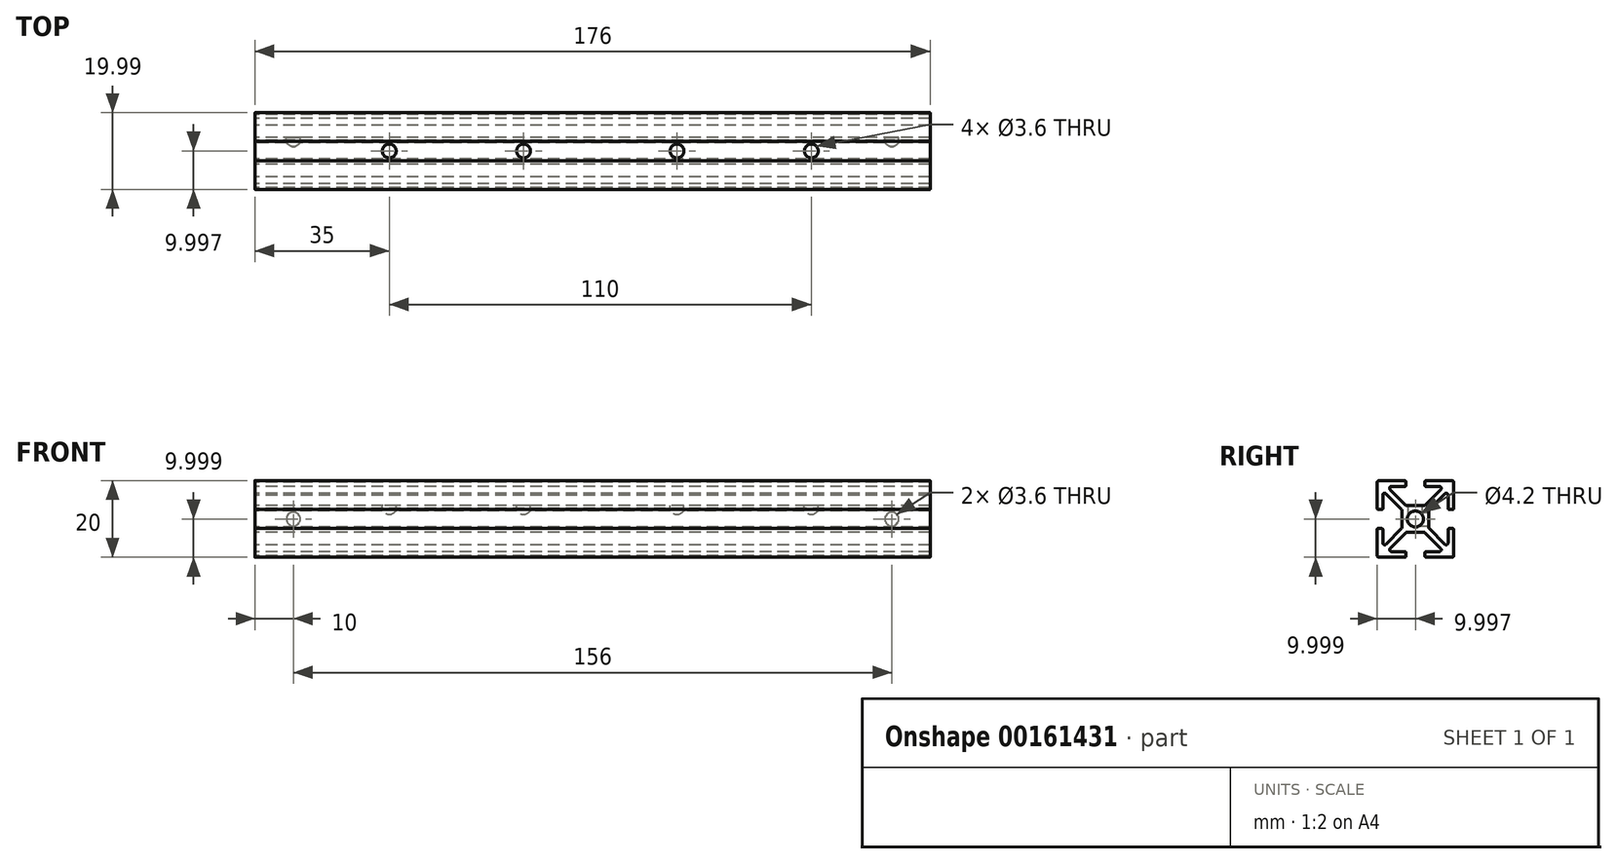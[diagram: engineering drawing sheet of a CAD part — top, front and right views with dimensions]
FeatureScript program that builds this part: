
annotation { "Feature Type Name" : "Feature", "Feature Type Description" : "" }
export const myFeature = defineFeature(function(context is Context, id is Id, definition is map)
    precondition{}
    {
        {
            var Q0;
            Q0=qCreatedBy(makeId("Right.planeOp"),FACE);
            var sketch = newSketch(context, id + "F0", { "sketchPlane" : qUnion([Q0])});
            skLineSegment(sketch, "E0.top", {"start": v(-10.52, -10.37) * mm, "end": v(-10.51, -10.37) * mm});
            skLineSegment(sketch, "E0.right", {"start": v(9.48, 9.63) * mm, "end": v(9.48, 9.63) * mm});
            skLineSegment(sketch, "E1.bottom", {"start": v(-3.26, 9.63) * mm, "end": v(-10.01, 9.63) * mm});
            skLineSegment(sketch, "E1.top", {"start": v(8.99, -10.37) * mm, "end": v(2.25, -10.37) * mm});
            skLineSegment(sketch, "E1.left", {"start": v(9.49, 9.13) * mm, "end": v(9.49, 2.38) * mm});
            skLineSegment(sketch, "E1.right", {"start": v(-10.51, -3.12) * mm, "end": v(-10.51, -9.87) * mm});
            skLineSegment(sketch, "E2", {"start": v(-10.51, 9.63) * mm, "end": v(-10.01, 9.13) * mm});
            skLineSegment(sketch, "E3", {"start": v(9.49, 9.63) * mm, "end": v(8.99, 9.13) * mm});
            skCircle(sketch, "E4", {"center": v(-0.51, -0.37) * mm, "radius": 2.1 * mm});
            skLineSegment(sketch, "E5.left", {"start": v(-3.01, 9.38) * mm, "end": v(-3.01, 8.38) * mm});
            skLineSegment(sketch, "E5.right", {"start": v(1.99, 9.38) * mm, "end": v(1.99, 8.38) * mm});
            skLineSegment(sketch, "E6", {"start": v(-4.01, 1.97) * mm, "end": v(-4.01, -2.7) * mm});
            skLineSegment(sketch, "E7", {"start": v(2.99, 1.97) * mm, "end": v(2.99, -2.7) * mm});
            skLineSegment(sketch, "E8", {"start": v(-6.75, -8.87) * mm, "end": v(-3.26, -8.87) * mm});
            skLineSegment(sketch, "E9", {"start": v(-9.01, -3.12) * mm, "end": v(-9.01, -6.6) * mm});
            skLineSegment(sketch, "E10", {"start": v(7.99, 5.86) * mm, "end": v(7.99, 2.38) * mm});
            skLineSegment(sketch, "E11", {"start": v(-6.75, 8.13) * mm, "end": v(-3.26, 8.13) * mm});
            skLineSegment(sketch, "E12.bottom", {"start": v(8.24, 2.13) * mm, "end": v(9.24, 2.13) * mm});
            skLineSegment(sketch, "E12.top", {"start": v(-10.26, -2.87) * mm, "end": v(-9.26, -2.87) * mm});
            skPoint(sketch, "E12.middle", {"position": v(9.49, -0.37) * mm});
            skLineSegment(sketch, "E13", {"start": v(-7.1, 7.28) * mm, "end": v(-3.03, 3.2) * mm});
            skLineSegment(sketch, "E14", {"start": v(2, -3.94) * mm, "end": v(6.07, -8.02) * mm});
            skLineSegment(sketch, "E15", {"start": v(6.07, 7.28) * mm, "end": v(2, 3.2) * mm});
            skLineSegment(sketch, "E16", {"start": v(-3.03, -3.94) * mm, "end": v(-7.1, -8.02) * mm});
            skArc(sketch, "E17.filletArc", {"start": v(-6.75, 8.13) * mm, "mid": v(-7.2, 7.82) * mm, "end": v(-7.1, 7.28) * mm});
            skPoint(sketch, "E18.newPointB", {"position": v(9.49, 8.13) * mm});
            skArc(sketch, "E18.filletArc", {"start": v(6.07, 7.28) * mm, "mid": v(6.18, 7.82) * mm, "end": v(5.72, 8.13) * mm});
            skArc(sketch, "E19.filletArc", {"start": v(7.99, 5.86) * mm, "mid": v(7.68, 6.32) * mm, "end": v(7.13, 6.22) * mm});
            skArc(sketch, "E20.filletArc", {"start": v(7.13, -6.96) * mm, "mid": v(7.68, -7.06) * mm, "end": v(7.99, -6.6) * mm});
            skArc(sketch, "E21.filletArc", {"start": v(5.72, -8.87) * mm, "mid": v(6.18, -8.56) * mm, "end": v(6.07, -8.02) * mm});
            skArc(sketch, "E22.filletArc", {"start": v(-7.1, -8.02) * mm, "mid": v(-7.2, -8.56) * mm, "end": v(-6.75, -8.87) * mm});
            skArc(sketch, "E23.filletArc", {"start": v(-9.01, -6.6) * mm, "mid": v(-8.7, -7.06) * mm, "end": v(-8.16, -6.96) * mm});
            skArc(sketch, "E24.filletArc", {"start": v(-8.16, 6.22) * mm, "mid": v(-8.73, 6.31) * mm, "end": v(-9, 5.8) * mm});
            skPoint(sketch, "E25.visualSharp", {"position": v(-10.51, 9.63) * mm});
            skArc(sketch, "E25.filletArc", {"start": v(-10.01, 9.63) * mm, "mid": v(-10.37, 9.48) * mm, "end": v(-10.51, 9.13) * mm});
            skPoint(sketch, "E26.visualSharp", {"position": v(9.49, 9.63) * mm});
            skArc(sketch, "E26.filletArc", {"start": v(9.49, 9.13) * mm, "mid": v(9.34, 9.48) * mm, "end": v(8.99, 9.63) * mm});
            skPoint(sketch, "E27.visualSharp", {"position": v(9.49, -10.37) * mm});
            skArc(sketch, "E27.filletArc", {"start": v(8.99, -10.37) * mm, "mid": v(9.34, -10.22) * mm, "end": v(9.49, -9.87) * mm});
            skPoint(sketch, "E28.visualSharp", {"position": v(-10.51, -10.37) * mm});
            skArc(sketch, "E28.filletArc", {"start": v(-10.51, -9.87) * mm, "mid": v(-10.37, -10.22) * mm, "end": v(-10.01, -10.37) * mm});
            skArc(sketch, "E29.filletArc", {"start": v(-3.26, 8.13) * mm, "mid": v(-3.09, 8.2) * mm, "end": v(-3.01, 8.38) * mm});
            skArc(sketch, "E30.filletArc", {"start": v(-9.01, -3.12) * mm, "mid": v(-9.09, -2.94) * mm, "end": v(-9.26, -2.87) * mm});
            skArc(sketch, "E31.filletArc", {"start": v(-3.01, 9.38) * mm, "mid": v(-3.09, 9.56) * mm, "end": v(-3.26, 9.63) * mm});
            skLineSegment(sketch, "E32", {"start": v(2.24, 9.63) * mm, "end": v(8.99, 9.63) * mm});
            skLineSegment(sketch, "E33", {"start": v(5.72, 8.13) * mm, "end": v(2.24, 8.13) * mm});
            skLineSegment(sketch, "E34", {"start": v(-9, 5.8) * mm, "end": v(-9, 2.38) * mm});
            skLineSegment(sketch, "E35", {"start": v(8.24, -2.87) * mm, "end": v(9.24, -2.87) * mm});
            skPoint(sketch, "E36.visualSharp", {"position": v(1.99, 8.13) * mm});
            skArc(sketch, "E36.filletArc", {"start": v(1.99, 8.38) * mm, "mid": v(2.06, 8.2) * mm, "end": v(2.24, 8.13) * mm});
            skPoint(sketch, "E37.visualSharp", {"position": v(1.99, 9.63) * mm});
            skArc(sketch, "E37.filletArc", {"start": v(2.24, 9.63) * mm, "mid": v(2.06, 9.56) * mm, "end": v(1.99, 9.38) * mm});
            skPoint(sketch, "E38.newPointB", {"position": v(-10.51, 2.13) * mm});
            skArc(sketch, "E38.filletArc", {"start": v(7.99, 2.38) * mm, "mid": v(8.06, 2.2) * mm, "end": v(8.24, 2.13) * mm});
            skLineSegment(sketch, "E39", {"start": v(7.99, -3.12) * mm, "end": v(7.99, -6.6) * mm});
            skPoint(sketch, "E40.visualSharp", {"position": v(7.99, -2.87) * mm});
            skArc(sketch, "E40.filletArc", {"start": v(8.24, -2.87) * mm, "mid": v(8.06, -2.94) * mm, "end": v(7.99, -3.12) * mm});
            skArc(sketch, "E41.filletArc", {"start": v(9.24, 2.13) * mm, "mid": v(9.41, 2.2) * mm, "end": v(9.49, 2.38) * mm});
            skLineSegment(sketch, "E42", {"start": v(9.49, -3.12) * mm, "end": v(9.49, -9.87) * mm});
            skPoint(sketch, "E43.visualSharp", {"position": v(9.49, -2.87) * mm});
            skArc(sketch, "E43.filletArc", {"start": v(9.49, -3.12) * mm, "mid": v(9.41, -2.94) * mm, "end": v(9.24, -2.87) * mm});
            skLineSegment(sketch, "E44", {"start": v(-9.26, 2.13) * mm, "end": v(-10.26, 2.13) * mm});
            skPoint(sketch, "E45.visualSharp", {"position": v(-9, 2.13) * mm});
            skArc(sketch, "E45.filletArc", {"start": v(-9.26, 2.13) * mm, "mid": v(-9.08, 2.2) * mm, "end": v(-9, 2.38) * mm});
            skPoint(sketch, "E46.newPointA", {"position": v(-10.51, -2.87) * mm});
            skArc(sketch, "E46.filletArc", {"start": v(-10.26, -2.87) * mm, "mid": v(-10.44, -2.94) * mm, "end": v(-10.51, -3.12) * mm});
            skLineSegment(sketch, "E47", {"start": v(-10.51, 2.38) * mm, "end": v(-10.51, 9.13) * mm});
            skArc(sketch, "E48.filletArc", {"start": v(-10.51, 2.38) * mm, "mid": v(-10.44, 2.2) * mm, "end": v(-10.26, 2.13) * mm});
            skPoint(sketch, "E49.newPointB", {"position": v(-3.01, 2.13) * mm});
            skLineSegment(sketch, "E50", {"start": v(7.13, -6.96) * mm, "end": v(3.06, -2.88) * mm});
            skPoint(sketch, "E50.endSnap0", {"position": v(2.99, -1.12) * mm});
            skPoint(sketch, "E51.newPointA", {"position": v(2.99, -2.8) * mm});
            skPoint(sketch, "E51.newPointB", {"position": v(2.99, -10.37) * mm});
            skArc(sketch, "E51.filletArc", {"start": v(2.99, -2.7) * mm, "mid": v(3, -2.8) * mm, "end": v(3.06, -2.88) * mm});
            skLineSegment(sketch, "E52", {"start": v(-2.85, -3.87) * mm, "end": v(1.82, -3.87) * mm});
            skArc(sketch, "E53.filletArc", {"start": v(2, -3.94) * mm, "mid": v(1.92, -3.89) * mm, "end": v(1.82, -3.87) * mm});
            skArc(sketch, "E54.filletArc", {"start": v(-2.85, -3.87) * mm, "mid": v(-2.94, -3.89) * mm, "end": v(-3.03, -3.94) * mm});
            skLineSegment(sketch, "E55", {"start": v(-8.16, -6.96) * mm, "end": v(-4.09, -2.88) * mm});
            skLineSegment(sketch, "E56", {"start": v(-8.16, 6.22) * mm, "end": v(-4.09, 2.14) * mm});
            skArc(sketch, "E57.filletArc", {"start": v(-4.01, 1.97) * mm, "mid": v(-4.03, 2.06) * mm, "end": v(-4.09, 2.14) * mm});
            skArc(sketch, "E58.filletArc", {"start": v(-4.09, -2.88) * mm, "mid": v(-4.03, -2.8) * mm, "end": v(-4.01, -2.7) * mm});
            skLineSegment(sketch, "E59", {"start": v(7.13, 6.22) * mm, "end": v(3.06, 2.14) * mm});
            skPoint(sketch, "E60.newPointB", {"position": v(2.99, 8.13) * mm});
            skArc(sketch, "E60.filletArc", {"start": v(3.06, 2.14) * mm, "mid": v(3, 2.06) * mm, "end": v(2.99, 1.97) * mm});
            skLineSegment(sketch, "E61", {"start": v(-2.85, 3.13) * mm, "end": v(1.82, 3.13) * mm});
            skArc(sketch, "E62.filletArc", {"start": v(-3.03, 3.2) * mm, "mid": v(-2.94, 3.15) * mm, "end": v(-2.85, 3.13) * mm});
            skArc(sketch, "E63.filletArc", {"start": v(1.82, 3.13) * mm, "mid": v(1.92, 3.15) * mm, "end": v(2, 3.2) * mm});
            skPoint(sketch, "E64.orphan", {"position": v(-3.01, 9.63) * mm});
            skPoint(sketch, "E65.orphan", {"position": v(-0.51, 9.63) * mm});
            skPoint(sketch, "E66.orphan", {"position": v(-10.51, -0.37) * mm});
            skLineSegment(sketch, "E67.trimOffspring", {"start": v(8.99, -9.87) * mm, "end": v(9.49, -10.37) * mm});
            skLineSegment(sketch, "E68.trimOffspring", {"start": v(-10.01, -9.87) * mm, "end": v(-10.51, -10.37) * mm});
            skPoint(sketch, "E69.trimOffspring.end.orphan", {"position": v(-0.51, -10.37) * mm});
            skLineSegment(sketch, "E70", {"start": v(2, 8.88) * mm, "end": v(2, 8.3) * mm});
            skPoint(sketch, "E70.startSnap0", {"position": v(1.99, 8.88) * mm});
            skLineSegment(sketch, "E71", {"start": v(-3.01, 8.88) * mm, "end": v(-3.01, 8.38) * mm});
            skPoint(sketch, "E72.start.orphan", {"position": v(-2.85, -8.87) * mm});
            skLineSegment(sketch, "E73.trimOffspring", {"start": v(2.25, -8.87) * mm, "end": v(5.72, -8.87) * mm});
            skLineSegment(sketch, "E74.trimOffspring", {"start": v(-3.26, -10.37) * mm, "end": v(-10.01, -10.37) * mm});
            skLineSegment(sketch, "E75.trimOffspring", {"start": v(2, -9.12) * mm, "end": v(2, -10.12) * mm});
            skLineSegment(sketch, "E76.trimOffspring", {"start": v(-3.01, -9.12) * mm, "end": v(-3.01, -10.12) * mm});
            skArc(sketch, "E77.filletArc", {"start": v(-3.01, -9.12) * mm, "mid": v(-3.09, -8.94) * mm, "end": v(-3.26, -8.87) * mm});
            skPoint(sketch, "E78.visualSharp", {"position": v(2, -8.87) * mm});
            skArc(sketch, "E78.filletArc", {"start": v(2.25, -8.87) * mm, "mid": v(2.07, -8.94) * mm, "end": v(2, -9.12) * mm});
            skPoint(sketch, "E79.visualSharp", {"position": v(-3.01, -10.37) * mm});
            skArc(sketch, "E79.filletArc", {"start": v(-3.26, -10.37) * mm, "mid": v(-3.09, -10.3) * mm, "end": v(-3.01, -10.12) * mm});
            skPoint(sketch, "E80.visualSharp", {"position": v(2, -10.37) * mm});
            skArc(sketch, "E80.filletArc", {"start": v(2, -10.12) * mm, "mid": v(2.07, -10.3) * mm, "end": v(2.25, -10.37) * mm});
            skLineSegment(sketch, "E81.trimOffspring", {"start": v(9.48, -3.08) * mm, "end": v(9.48, -9.93) * mm});
            skLineSegment(sketch, "E82.trimOffspring", {"start": v(2.24, -10.37) * mm, "end": v(9, -10.37) * mm});
            skLineSegment(sketch, "E83", {"start": v(-10.51, -9.87) * mm, "end": v(-10.51, -3.12) * mm});
            skLineSegment(sketch, "E84", {"start": v(-10.51, 9.13) * mm, "end": v(-10.51, 2.38) * mm});
            skLineSegment(sketch, "E85.trimOffspring", {"start": v(9.48, 9.19) * mm, "end": v(9.48, 2.34) * mm});
            skLineSegment(sketch, "E86.trimOffspring", {"start": v(9.48, -10.37) * mm, "end": v(9.48, -10.37) * mm});
            skLineSegment(sketch, "E87.trimOffspring", {"start": v(-10.03, -10.37) * mm, "end": v(-3.25, -10.37) * mm});
            skSolve(sketch);
        }
        {
            var Q0;
            Q0=makeQuery(id+"F0.imprint","IMPRINT",FACE,{"disambiguationData":[TD([[makeQuery(id+"F0.imprint","IMPRINT",EDGE,{"derivedFrom":sQuery(id+"F0.wireOp",EDGE,"E4")}),-1.0]])]});
            extrude(context, id + "F1", {"entities" : qUnion([Q0]), "depth" : 176 * mm});
        }
        {
            var Q0;
            Q0=makeQuery(id+"F1.opExtrude","SWEPT_FACE",FACE,{"disambiguationData":[OSD([sQuery(id+"F0.wireOp",EDGE,"E61")])]});
            var sketch = newSketch(context, id + "F2", { "sketchPlane" : qUnion([Q0])});
            skPoint(sketch, "E88", {"position": v(0, -0.51) * mm});
            skLineSegment(sketch, "E89", {"start": v(0, -0.51) * mm, "end": v(145, -0.51) * mm});
            skPoint(sketch, "E90", {"position": v(176, -0.51) * mm});
            skPoint(sketch, "E91", {"position": v(145, -0.51) * mm});
            skPoint(sketch, "E92", {"position": v(35, -0.51) * mm});
            skPoint(sketch, "E93", {"position": v(70, -0.51) * mm});
            skPoint(sketch, "E94", {"position": v(110, -0.51) * mm});
            skCircle(sketch, "E95", {"center": v(35, -0.51) * mm, "radius": 1.8 * mm});
            skCircle(sketch, "E96", {"center": v(70, -0.51) * mm, "radius": 1.8 * mm});
            skCircle(sketch, "E97", {"center": v(110, -0.51) * mm, "radius": 1.8 * mm});
            skCircle(sketch, "E98", {"center": v(145, -0.51) * mm, "radius": 1.8 * mm});
            skSolve(sketch);
        }
        {
            var Q0;
            Q0 = qSketchRegion(id + "F2", true);
            extrude(context, id + "F3", {"entities" : qUnion([Q0]), "operationType" : NewBodyOperationType.REMOVE, "oppositeDirection" : true, "depth" : 3 * mm});
        }
        {
            var Q0;
            Q0=makeQuery(id+"F1.opExtrude","SWEPT_FACE",FACE,{"disambiguationData":[OSD([sQuery(id+"F0.wireOp",EDGE,"E7")])]});
            var sketch = newSketch(context, id + "F4", { "sketchPlane" : qUnion([Q0])});
            skPoint(sketch, "E99", {"position": v(-176, -0.37) * mm});
            skPoint(sketch, "E100", {"position": v(-166, -0.37) * mm});
            skPoint(sketch, "E101", {"position": v(-10, -0.37) * mm});
            skCircle(sketch, "E102", {"center": v(-166, -0.37) * mm, "radius": 1.8 * mm});
            skCircle(sketch, "E103", {"center": v(-10, -0.37) * mm, "radius": 1.8 * mm});
            skSolve(sketch);
        }
        {
            var Q0;
            Q0 = qSketchRegion(id + "F4", true);
            extrude(context, id + "F5", {"entities" : qUnion([Q0]), "operationType" : NewBodyOperationType.REMOVE, "oppositeDirection" : true, "depth" : 3 * mm});
        }
    });
